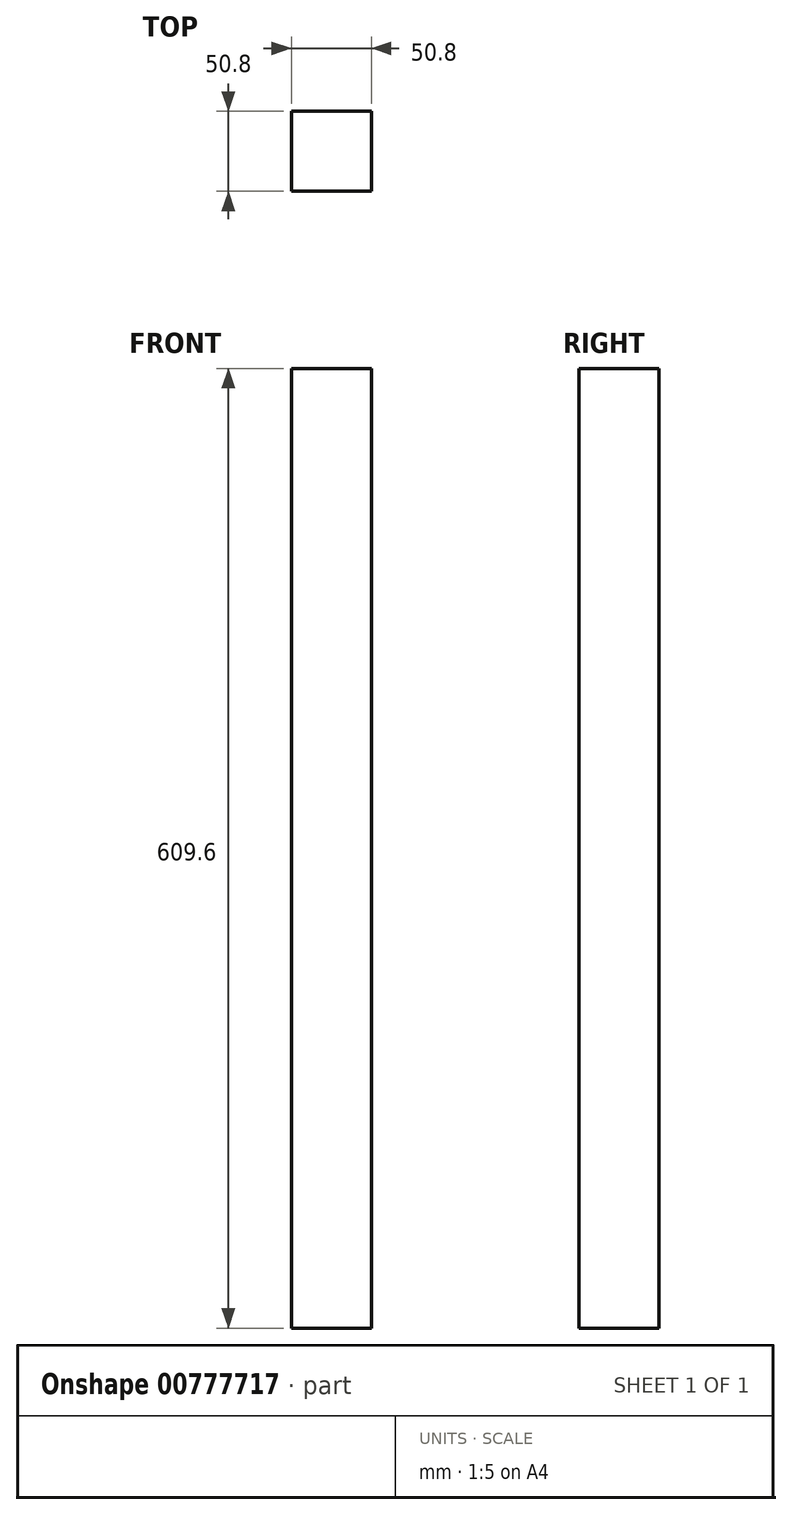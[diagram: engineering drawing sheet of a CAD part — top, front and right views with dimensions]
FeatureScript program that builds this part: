
annotation { "Feature Type Name" : "Feature", "Feature Type Description" : "" }
export const myFeature = defineFeature(function(context is Context, id is Id, definition is map)
    precondition{}
    {
        {
            var Q0;
            Q0=qCreatedBy(makeId("Top.planeOp"),FACE);
            var sketch = newSketch(context, id + "F0", { "sketchPlane" : qUnion([Q0])});
            skLineSegment(sketch, "E0.bottom", {"start": v(0, 0) * mm, "end": v(50.8, 0) * mm});
            skLineSegment(sketch, "E0.top", {"start": v(0, 50.8) * mm, "end": v(50.8, 50.8) * mm});
            skLineSegment(sketch, "E0.left", {"start": v(0, 0) * mm, "end": v(0, 50.8) * mm});
            skLineSegment(sketch, "E0.right", {"start": v(50.8, 0) * mm, "end": v(50.8, 50.8) * mm});
            skSolve(sketch);
        }
        {
            var Q0;
            Q0 = qSketchRegion(id + "F0", true);
            extrude(context, id + "F1", {"entities" : qUnion([Q0]), "depth" : 609.6 * mm, "offsetDistance" : 25.4 * mm});
        }
    });
